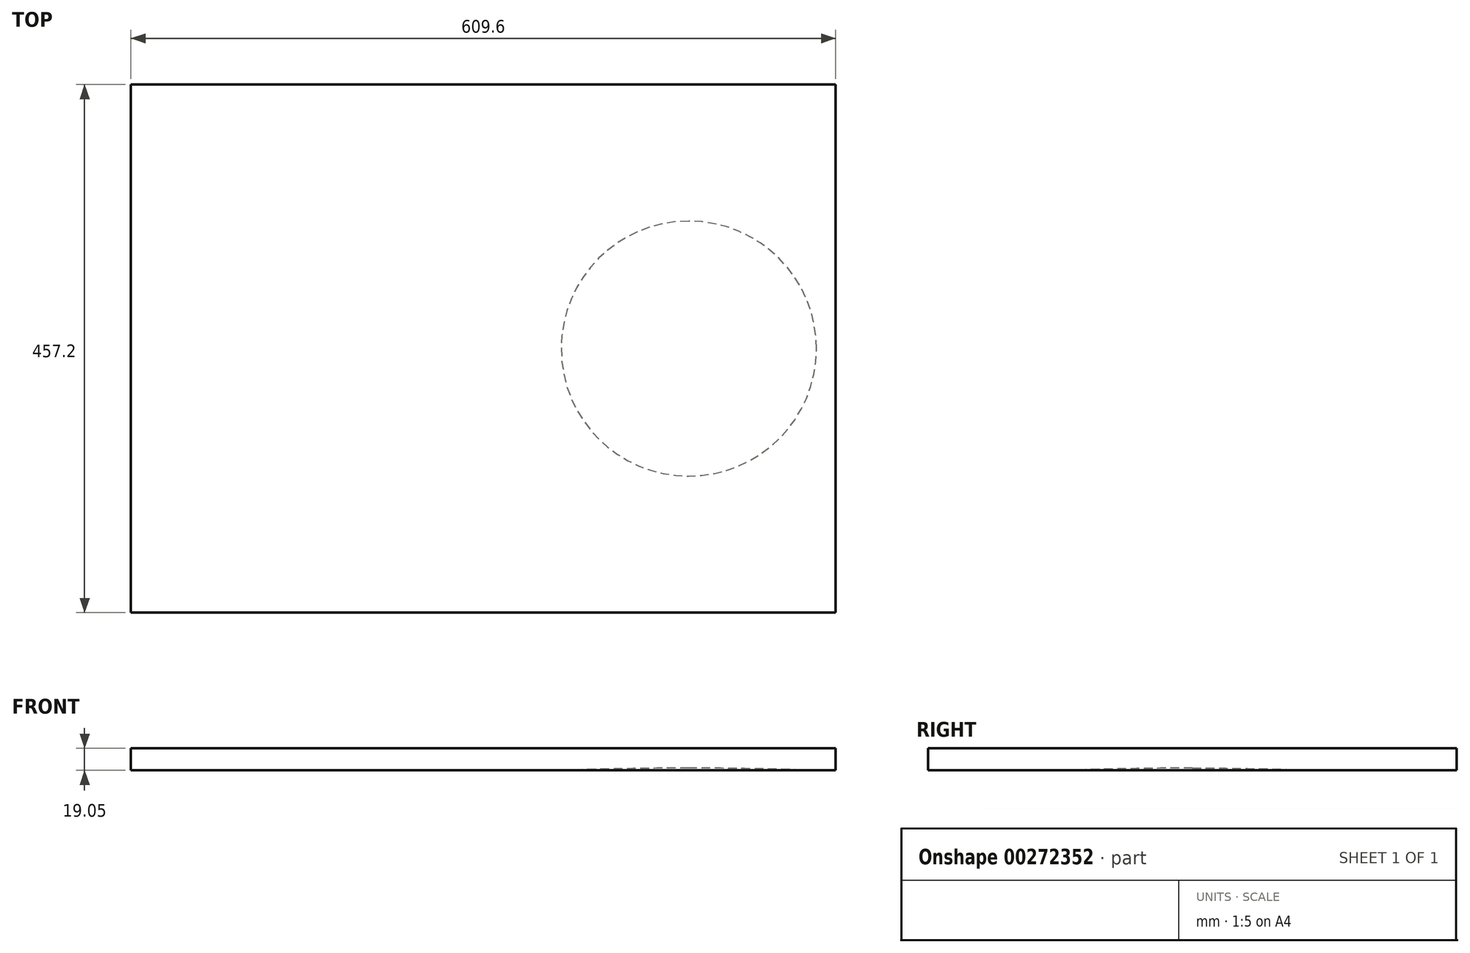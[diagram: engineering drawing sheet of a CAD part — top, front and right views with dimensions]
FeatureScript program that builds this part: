
annotation { "Feature Type Name" : "Feature", "Feature Type Description" : "" }
export const myFeature = defineFeature(function(context is Context, id is Id, definition is map)
    precondition{}
    {
        {
            var Q0;
            Q0=qCreatedBy(makeId("Top.planeOp"),FACE);
            var sketch = newSketch(context, id + "F0", { "sketchPlane" : qUnion([Q0])});
            skLineSegment(sketch, "E0.bottom", {"start": v(304.8, -228.6) * mm, "end": v(-304.8, -228.6) * mm});
            skLineSegment(sketch, "E0.top", {"start": v(304.8, 228.6) * mm, "end": v(-304.8, 228.6) * mm});
            skLineSegment(sketch, "E0.left", {"start": v(304.8, -228.6) * mm, "end": v(304.8, 228.6) * mm});
            skLineSegment(sketch, "E0.right", {"start": v(-304.8, -228.6) * mm, "end": v(-304.8, 228.6) * mm});
            skPoint(sketch, "E0.middle", {"position": v(0, 0) * mm});
            skSolve(sketch);
        }
        {
            var Q0;
            Q0=makeQuery(id+"F0.imprint","IMPRINT",FACE,{"disambiguationData":[TD([[makeQuery(id+"F0.imprint","IMPRINT",EDGE,{"derivedFrom":sQuery(id+"F0.wireOp",EDGE,"E0.bottom")}),-1.0]])]});
            extrude(context, id + "F1", {"entities" : qUnion([Q0]), "oppositeDirection" : true, "depth" : 19.05 * mm, "offsetDistance" : 25.4 * mm});
        }
        {
            var Q0;
            Q0=qCreatedBy(makeId("Right.planeOp"),FACE);
            cPlane(context, id + "F2", {"entities" : qUnion([Q0]), "cplaneType" : CPlaneType.OFFSET, "offset" : 177.8 * mm, "width" : 152.4 * mm, "height" : 152.4 * mm});
        }
        {
            var Q0;
            Q0=qCreatedBy(id+"F2.planeOp",FACE);
            var sketch = newSketch(context, id + "F3", { "sketchPlane" : qUnion([Q0])});
            skLineSegment(sketch, "E1", {"start": v(0, -17.05) * mm, "end": v(0, -3065.05) * mm});
            skLineSegment(sketch, "E2", {"start": v(0, -3065.05) * mm, "end": v(458.6, -51.75) * mm});
            skArc(sketch, "E3", {"start": v(0, -17.05) * mm, "mid": v(229.95, -25.74) * mm, "end": v(458.6, -51.75) * mm});
            skPoint(sketch, "E4.orphan", {"position": v(466.47, 0) * mm});
            skSolve(sketch);
        }
        {
            var Q0;
            Q0=makeQuery(id+"F3.imprint","IMPRINT",FACE,{"disambiguationData":[TD([[makeQuery(id+"F3.imprint","IMPRINT",EDGE,{"derivedFrom":sQuery(id+"F3.wireOp",EDGE,"E1")}),1.0]])]});
            var Q1;
            Q1=sQuery(id+"F3.wireOp",EDGE,"E1");
            revolve(context, id + "F4", {"operationType" : NewBodyOperationType.REMOVE, "entities" : qUnion([Q0]), "axis" : qUnion([Q1]), "revolveType" : RevolveType.FULL, "oppositeDirection" : true});
        }
    });
